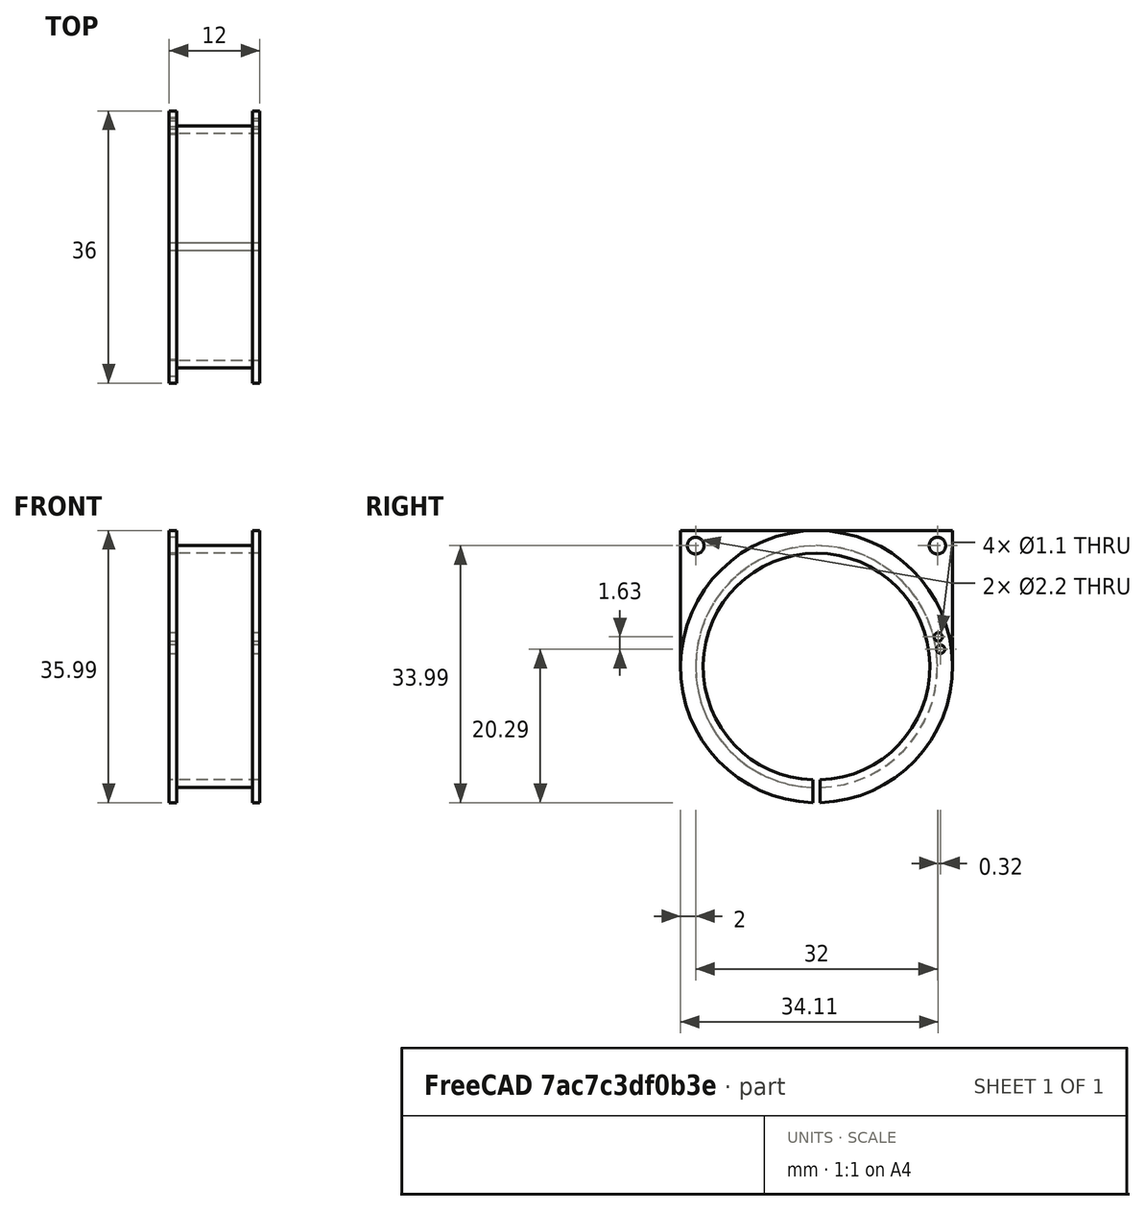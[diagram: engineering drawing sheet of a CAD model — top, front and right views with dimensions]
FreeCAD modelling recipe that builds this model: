
FCSTD DOCUMENT  (FreeCAD 0.20R29603 (Git))
Label: Quak_XL30_PCBHolder01_ModulationCoil
License: All rights reserved
LicenseURL: http://en.wikipedia.org/wiki/All_rights_reserved
objects: Part::Cylinder×11, Part::Cut×8, Part::MultiFuse×4, Part::Box×2
note: 25 computed .brp shape members not serialized (recipe doc carries the construction recipe); baked Part::Feature solids carry a one-line shape summary decoded from their .brp

FEATURE [Part::Box] Box038  label="Würfel037"
  AttacherType = Attacher::AttachEngine3D
  Height = 5
  Length = 12
  Placement = pos=(-17,-0.5,-19) rot=(0,0,1;0rad)
  Width = 1
FEATURE [Part::Box] Box039  label="Würfel038"
  AttacherType = Attacher::AttachEngine3D
  Height = 18
  Length = 1
  Placement = pos=(-17,-18,0) rot=(0,0,1;0rad)
  Width = 36
FEATURE [Part::Cylinder] Cylinder066  label="Zylinder063"
  Angle = 360
  AttacherType = Attacher::AttachEngine3D
  FirstAngle = 0
  Height = 12
  Placement = pos=(0,0,0) rot=(0,1,0;1.5708rad)
  Radius = 18
  SecondAngle = 0
FEATURE [Part::Cylinder] Cylinder067  label="Zylinder064"
  Angle = 360
  AttacherType = Attacher::AttachEngine3D
  FirstAngle = 0
  Height = 12
  Placement = pos=(0,0,0) rot=(0,1,0;1.5708rad)
  Radius = 15
  SecondAngle = 0
FEATURE [Part::Cut] Cut049
  Base = -> Cylinder066
  Placement = pos=(-17,0,0) rot=(0,0,1;0rad)
  Tool = -> Cylinder067
FEATURE [Part::Cylinder] Cylinder068  label="Zylinder065"
  Angle = 360
  AttacherType = Attacher::AttachEngine3D
  FirstAngle = 0
  Height = 10
  Placement = pos=(0,0,0) rot=(0,1,0;1.5708rad)
  Radius = 18
  SecondAngle = 0
FEATURE [Part::Cylinder] Cylinder069  label="Zylinder066"
  Angle = 360
  AttacherType = Attacher::AttachEngine3D
  FirstAngle = 0
  Height = 10
  Placement = pos=(0,0,0) rot=(0,1,0;1.5708rad)
  Radius = 16
  SecondAngle = 0
FEATURE [Part::Cut] Cut050
  Base = -> Cylinder068
  Placement = pos=(-16,0,0) rot=(0,0,1;0rad)
  Tool = -> Cylinder069
FEATURE [Part::Cut] Cut051
  Base = -> Cut049
  Tool = -> Cut050
FEATURE [Part::Cut] Cut054
  Base = -> Cut051
  Tool = -> Box038
FEATURE [Part::Cylinder] Cylinder071  label="Zylinder068"
  Angle = 360
  AttacherType = Attacher::AttachEngine3D
  FirstAngle = 0
  Height = 1
  Placement = pos=(-17,-16,16) rot=(0,1,0;1.5708rad)
  Radius = 1.1
  SecondAngle = 0
FEATURE [Part::Cylinder] Cylinder072  label="Zylinder069"
  Angle = 360
  AttacherType = Attacher::AttachEngine3D
  FirstAngle = 0
  Height = 1
  Placement = pos=(-17,16,16) rot=(0,1,0;1.5708rad)
  Radius = 1.1
  SecondAngle = 0
FEATURE [Part::Cylinder] Cylinder073  label="Zylinder070"
  Angle = 360
  AttacherType = Attacher::AttachEngine3D
  FirstAngle = 0
  Height = 12
  Placement = pos=(-17,0,0) rot=(0,1,0;1.5708rad)
  Radius = 15
  SecondAngle = 0
FEATURE [Part::Cylinder] Cylinder074  label="Zylinder071"
  Angle = 360
  AttacherType = Attacher::AttachEngine3D
  FirstAngle = 0
  Height = 12
  Placement = pos=(-17,16.43,2.3) rot=(0,1,0;1.5708rad)
  Radius = 0.55
  SecondAngle = 0
FEATURE [Part::Cylinder] Cylinder075  label="Zylinder072"
  Angle = 360
  AttacherType = Attacher::AttachEngine3D
  FirstAngle = 0
  Height = 12
  Placement = pos=(-17,16.11,3.93) rot=(0,1,0;1.5708rad)
  Radius = 0.55
  SecondAngle = 0
FEATURE [Part::Cylinder] Cylinder078  label="Zylinder075"
  Angle = 360
  AttacherType = Attacher::AttachEngine3D
  FirstAngle = 0
  Height = 12
  Placement = pos=(-17,16.43,2.3) rot=(0,1,0;1.5708rad)
  Radius = 0.55
  SecondAngle = 0
FEATURE [Part::Cylinder] Cylinder079  label="Zylinder076"
  Angle = 360
  AttacherType = Attacher::AttachEngine3D
  FirstAngle = 0
  Height = 12
  Placement = pos=(-17,16.11,3.93) rot=(0,1,0;1.5708rad)
  Radius = 0.55
  SecondAngle = 0
FEATURE [Part::MultiFuse] Fusion034
  Shapes = -> [Cylinder071,Cylinder072]
FEATURE [Part::Cut] Cut055
  Base = -> Box039
  Tool = -> Fusion034
FEATURE [Part::Cut] Cut056
  Base = -> Cut055
  Tool = -> Cylinder073
FEATURE [Part::MultiFuse] Fusion035
  Shapes = -> [Cylinder074,Cylinder075]
FEATURE [Part::Cut] Cut057
  Base = -> Cut054
  Tool = -> Fusion035
FEATURE [Part::MultiFuse] Fusion037
  Shapes = -> [Cylinder078,Cylinder079]
FEATURE [Part::Cut] Cut059
  Base = -> Cut056
  Tool = -> Fusion037
FEATURE [Part::MultiFuse] Fusion038
  Shapes = -> [Cut057,Cut059]
